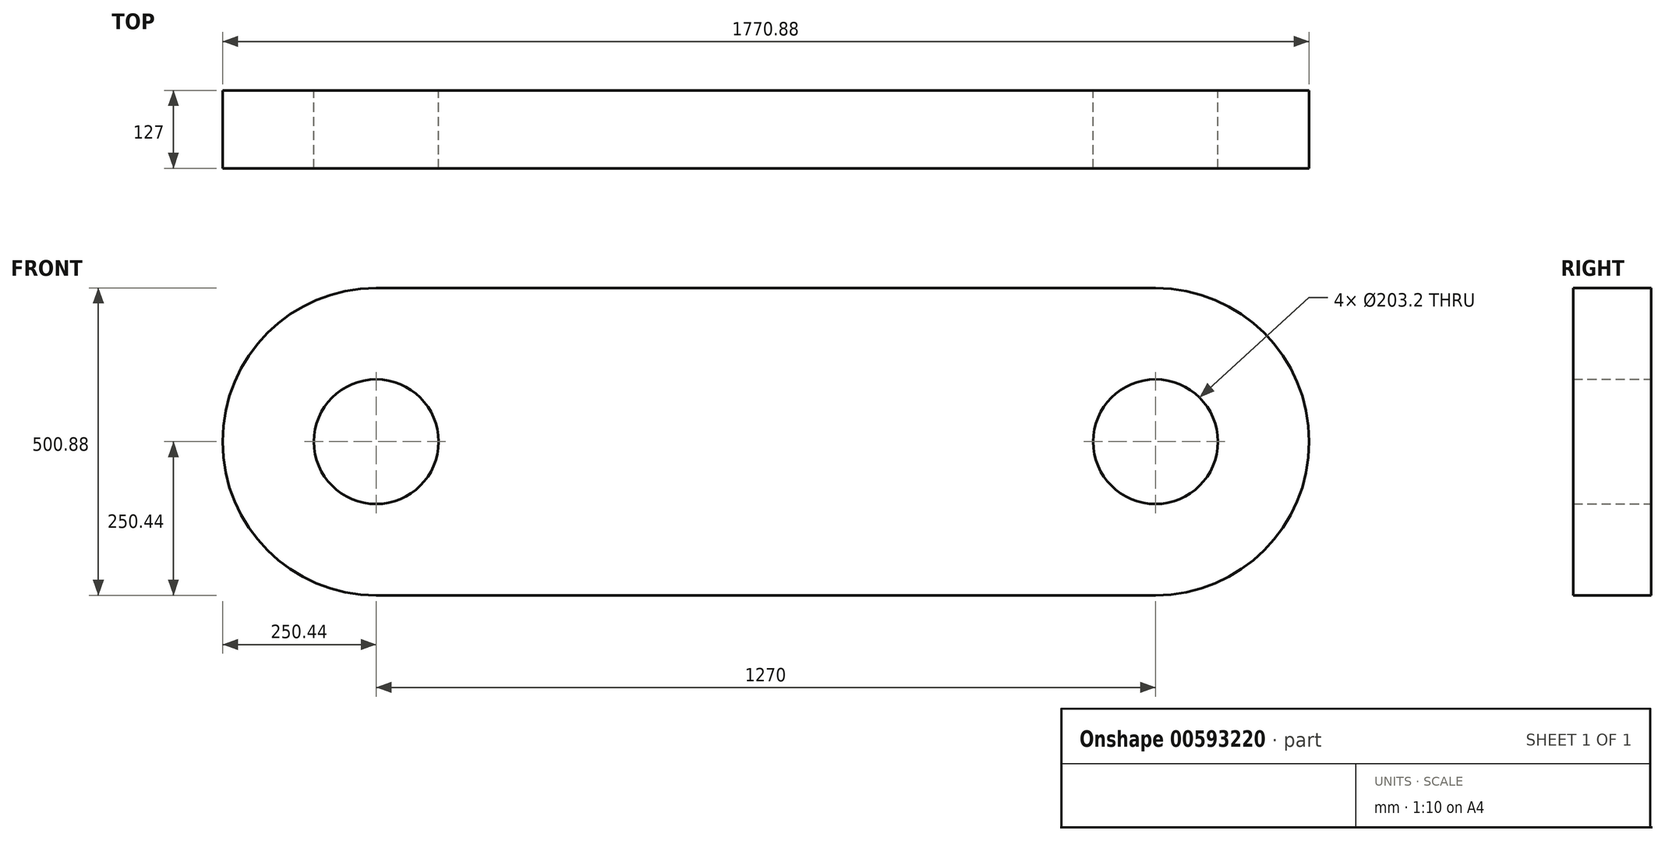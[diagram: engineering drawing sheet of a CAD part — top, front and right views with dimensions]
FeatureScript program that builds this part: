
annotation { "Feature Type Name" : "Feature", "Feature Type Description" : "" }
export const myFeature = defineFeature(function(context is Context, id is Id, definition is map)
    precondition{}
    {
        {
            var Q0;
            Q0=qCreatedBy(makeId("Front.planeOp"),FACE);
            var sketch = newSketch(context, id + "F0", { "sketchPlane" : qUnion([Q0])});
            skLineSegment(sketch, "E0.bottom", {"start": v(-635, 250.44) * mm, "end": v(635, 250.44) * mm});
            skLineSegment(sketch, "E0.top", {"start": v(-635, -250.44) * mm, "end": v(635, -250.44) * mm});
            skLineSegment(sketch, "E0.left", {"start": v(-635, 250.44) * mm, "end": v(-635, -250.44) * mm});
            skLineSegment(sketch, "E0.right", {"start": v(635, 250.44) * mm, "end": v(635, -250.44) * mm});
            skCircle(sketch, "E1", {"center": v(635, 0) * mm, "radius": 250.44 * mm});
            skCircle(sketch, "E2", {"center": v(-635, 0) * mm, "radius": 250.44 * mm});
            skCircle(sketch, "E3", {"center": v(-635, 0) * mm, "radius": 101.6 * mm});
            skCircle(sketch, "E4", {"center": v(635, 0) * mm, "radius": 101.6 * mm});
            skSolve(sketch);
        }
        {
            var Q0;
            {var subQ0=sQuery(id+"F0.wireOp",EDGE,"E0.bottom");Q0=makeQuery(id+"F0.imprint","IMPRINT",FACE,{"disambiguationData":[TD([[makeQuery(id+"F0.imprint","IMPRINT",EDGE,{"derivedFrom":subQ0}),-1.0]])]});}
            var Q1;
            {var subQ1=sQuery(id+"F0.wireOp",EDGE,"E0.left");var subQ3=sQuery(id+"F0.wireOp",EDGE,"E3");var subQ4=makeQuery(id+"F0.imprint","INTERSECT",VERTEX,{"disambiguationData":[OD(0.0)],"derivedFrom":[subQ1,subQ3]});Q1=makeQuery(id+"F0.imprint","IMPRINT",FACE,{"disambiguationData":[TD([[makeQuery(id+"F0.imprint","IMPRINT",EDGE,{"disambiguationData":[TD([[subQ4,1.0]])],"derivedFrom":subQ3}),-1.0]])]});}
            var Q2;
            {var subQ1=sQuery(id+"F0.wireOp",EDGE,"E0.left");var subQ3=sQuery(id+"F0.wireOp",EDGE,"E3");var subQ4=makeQuery(id+"F0.imprint","INTERSECT",VERTEX,{"disambiguationData":[OD(0.0)],"derivedFrom":[subQ1,subQ3]});Q2=makeQuery(id+"F0.imprint","IMPRINT",FACE,{"disambiguationData":[TD([[makeQuery(id+"F0.imprint","IMPRINT",EDGE,{"disambiguationData":[TD([[subQ4,-1.0]])],"derivedFrom":subQ3}),-1.0]])]});}
            var Q3;
            {var subQ1=sQuery(id+"F0.wireOp",EDGE,"E0.right");var subQ3=sQuery(id+"F0.wireOp",EDGE,"E4");var subQ4=makeQuery(id+"F0.imprint","INTERSECT",VERTEX,{"disambiguationData":[OD(0.0)],"derivedFrom":[subQ1,subQ3]});Q3=makeQuery(id+"F0.imprint","IMPRINT",FACE,{"disambiguationData":[TD([[makeQuery(id+"F0.imprint","IMPRINT",EDGE,{"disambiguationData":[TD([[subQ4,1.0]])],"derivedFrom":subQ3}),-1.0]])]});}
            var Q4;
            {var subQ1=sQuery(id+"F0.wireOp",EDGE,"E0.right");var subQ3=sQuery(id+"F0.wireOp",EDGE,"E4");var subQ4=makeQuery(id+"F0.imprint","INTERSECT",VERTEX,{"disambiguationData":[OD(0.0)],"derivedFrom":[subQ1,subQ3]});Q4=makeQuery(id+"F0.imprint","IMPRINT",FACE,{"disambiguationData":[TD([[makeQuery(id+"F0.imprint","IMPRINT",EDGE,{"disambiguationData":[TD([[subQ4,-1.0]])],"derivedFrom":subQ3}),-1.0]])]});}
            extrude(context, id + "F1", {"entities" : qUnion([Q0, Q1, Q2, Q3, Q4]), "depth" : 127 * mm, "offsetDistance" : 25.4 * mm});
        }
    });
